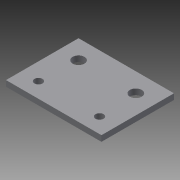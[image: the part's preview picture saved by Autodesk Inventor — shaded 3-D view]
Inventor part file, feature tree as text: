
AUTODESK INVENTOR PART (.ipt)
format: ipt  version: 2015 (Build 190159000, 159)  size: 96,256 bytes
history: native  units: mm
features: sketch x3, hole x2, other x1, extrude x1
ambient origin geometry x8: Origin, YZ Plane, XZ Plane, XY Plane, X Axis, Y Axis, Z Axis, Center Point
bodies: Body1 (feature_tree)
feature tree (7):
  other  "ソリッド1"
  extrude  "押し出し1"  Depth=25.0mm
  hole  "穴1"  [1 undecoded]
  hole  "穴2"  [1 undecoded]
  sketch  "スケッチ1"
  sketch  "スケッチ2"
  sketch  "スケッチ3"
note: 2 required parameter values undecoded (feature->parameter linkage not recoverable at this tier; creation-order binding heuristic only, values carry confidence <= 0.55)
